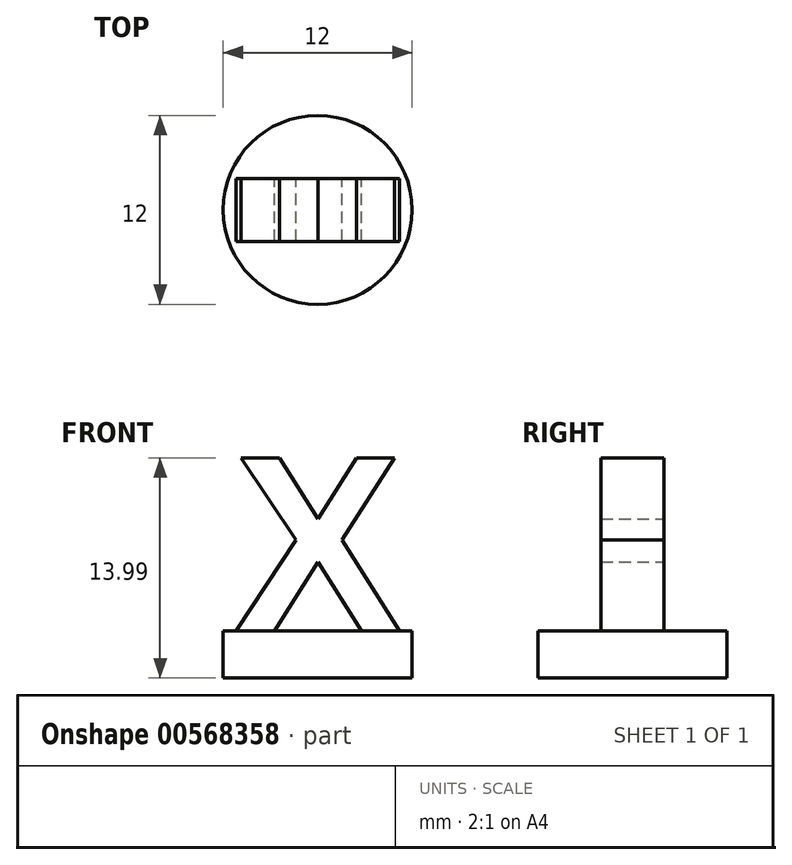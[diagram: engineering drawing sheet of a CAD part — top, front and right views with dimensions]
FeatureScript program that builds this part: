
annotation { "Feature Type Name" : "Feature", "Feature Type Description" : "" }
export const myFeature = defineFeature(function(context is Context, id is Id, definition is map)
    precondition{}
    {
        {
            var Q0;
            Q0=qCreatedBy(makeId("Top.planeOp"),FACE);
            var sketch = newSketch(context, id + "F0", { "sketchPlane" : qUnion([Q0])});
            skCircle(sketch, "E0", {"center": v(0, 0) * mm, "radius": 6 * mm});
            skSolve(sketch);
        }
        {
            var Q0;
            Q0 = qSketchRegion(id + "F0", true);
            extrude(context, id + "F1", {"entities" : qUnion([Q0]), "oppositeDirection" : true, "depth" : 3 * mm, "offsetDistance" : 25 * mm});
        }
        {
            var Q0;
            Q0=qCreatedBy(makeId("Front.planeOp"),FACE);
            var sketch = newSketch(context, id + "F2", { "sketchPlane" : qUnion([Q0])});
            skText(sketch, "E1", { "text": "X", "fontName": "Arimo-Bold.ttf"});
            const initialGuessF2  = {"E1": [-0.00532, 0, 1, 0, 0.0115]};
            skSetInitialGuess(sketch, initialGuessF2);
            skSolve(sketch);
        }
        {
            var Q0;
            Q0 = qSketchRegion(id + "F2", true);
            extrude(context, id + "F3", {"entities" : qUnion([Q0]), "operationType" : NewBodyOperationType.ADD, "depth" : 2 * mm, "offsetDistance" : 25 * mm, "hasSecondDirection" : true, "secondDirectionOppositeDirection" : true, "secondDirectionDepth" : 2 * mm});
        }
    });
